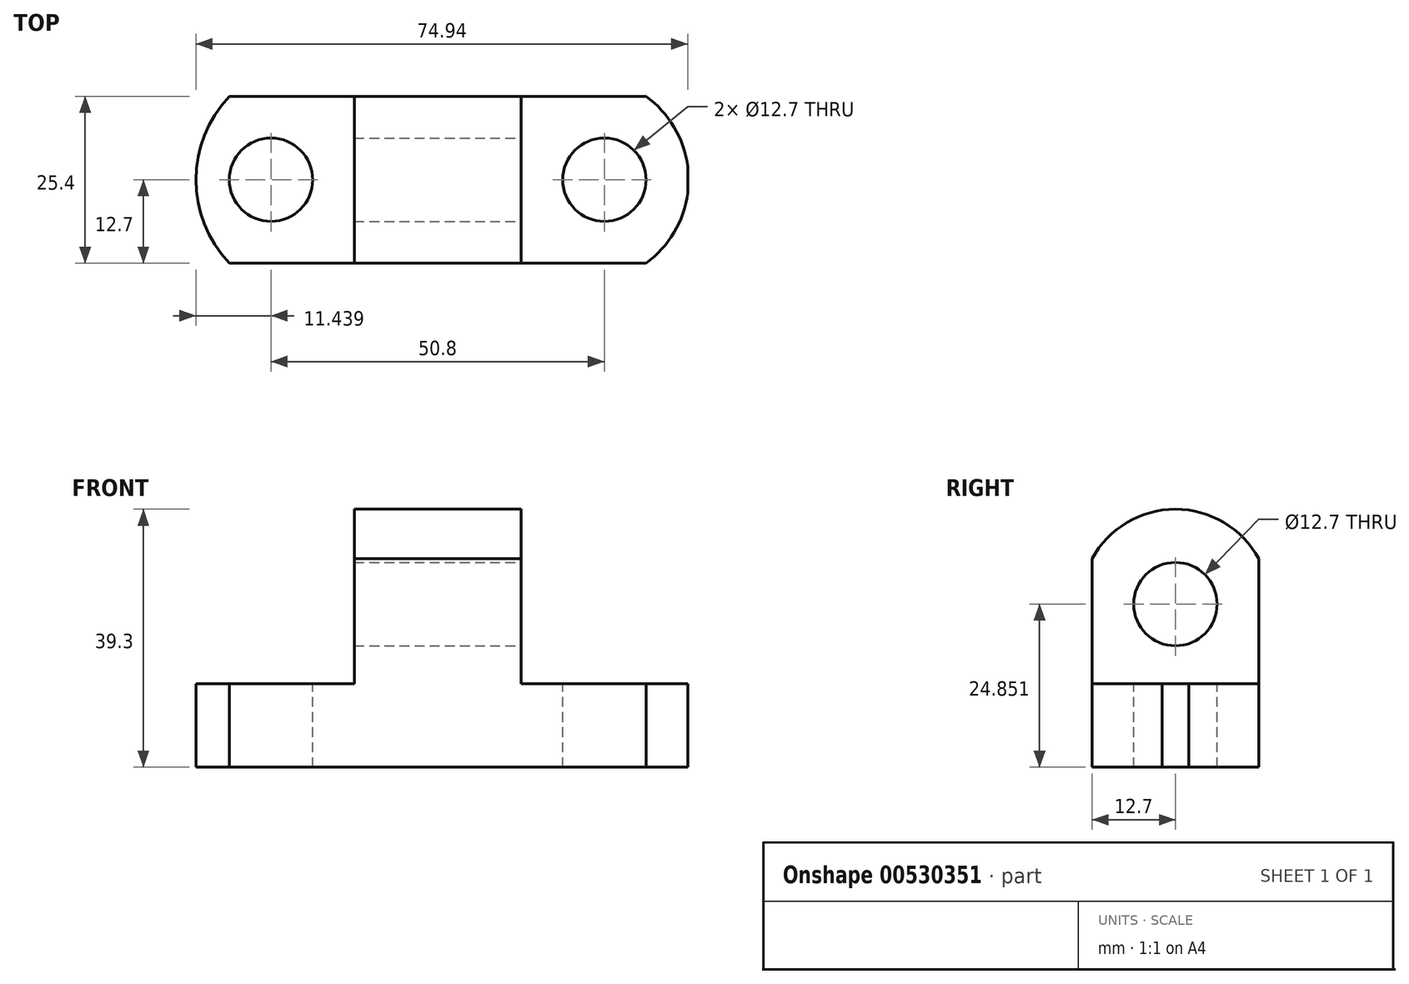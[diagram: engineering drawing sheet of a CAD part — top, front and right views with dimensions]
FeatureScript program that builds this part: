
annotation { "Feature Type Name" : "Feature", "Feature Type Description" : "" }
export const myFeature = defineFeature(function(context is Context, id is Id, definition is map)
    precondition{}
    {
        {
            var Q0;
            Q0=qCreatedBy(makeId("Front.planeOp"),FACE);
            var sketch = newSketch(context, id + "F0", { "sketchPlane" : qUnion([Q0])});
            skLineSegment(sketch, "E0", {"start": v(-46.07, 12.7) * mm, "end": v(-46.07, 0) * mm});
            skLineSegment(sketch, "E1", {"start": v(-46.07, 0) * mm, "end": v(30.13, 0) * mm});
            skLineSegment(sketch, "E2", {"start": v(30.13, 0) * mm, "end": v(30.13, 12.7) * mm});
            skLineSegment(sketch, "E3", {"start": v(30.13, 12.7) * mm, "end": v(4.73, 12.7) * mm});
            skLineSegment(sketch, "E4", {"start": v(4.73, 12.7) * mm, "end": v(4.73, 44.45) * mm});
            skLineSegment(sketch, "E5", {"start": v(4.73, 44.45) * mm, "end": v(-20.67, 44.45) * mm});
            skLineSegment(sketch, "E6", {"start": v(-20.67, 44.45) * mm, "end": v(-20.67, 12.7) * mm});
            skLineSegment(sketch, "E7", {"start": v(-20.67, 12.7) * mm, "end": v(-46.07, 12.7) * mm});
            skSolve(sketch);
        }
        {
            var Q0;
            Q0 = qSketchRegion(id + "F0", true);
            extrude(context, id + "F1", {"entities" : qUnion([Q0]), "depth" : 25.4 * mm, "offsetDistance" : 25.4 * mm});
        }
        {
            var Q0;
            Q0=makeQuery(id+"F1.opExtrude","SWEPT_FACE",FACE,{"disambiguationData":[OSD([sQuery(id+"F0.wireOp",EDGE,"E7")])]});
            var sketch = newSketch(context, id + "F2", { "sketchPlane" : qUnion([Q0])});
            skCircle(sketch, "E8", {"center": v(-33.37, -12.7) * mm, "radius": 6.35 * mm});
            skCircle(sketch, "E9", {"center": v(17.43, -12.7) * mm, "radius": 6.35 * mm});
            skSolve(sketch);
        }
        {
            var Q0;
            Q0=makeQuery(id+"F2.imprint","IMPRINT",FACE,{"disambiguationData":[TD([[makeQuery(id+"F2.imprint","IMPRINT",EDGE,{"derivedFrom":sQuery(id+"F2.wireOp",EDGE,"E9")}),1.0]])]});
            var Q1;
            Q1=makeQuery(id+"F2.imprint","IMPRINT",FACE,{"disambiguationData":[TD([[makeQuery(id+"F2.imprint","IMPRINT",EDGE,{"derivedFrom":sQuery(id+"F2.wireOp",EDGE,"E8")}),1.0]])]});
            extrude(context, id + "F3", {"entities" : qUnion([Q0, Q1]), "operationType" : NewBodyOperationType.REMOVE, "endBound" : BoundingType.THROUGH_ALL, "oppositeDirection" : true, "depth" : 25.4 * mm, "offsetDistance" : 25.4 * mm});
        }
        {
            var Q0;
            Q0=makeQuery(id+"F1.opExtrude","SWEPT_FACE",FACE,{"disambiguationData":[OSD([sQuery(id+"F0.wireOp",EDGE,"E4")])]});
            var sketch = newSketch(context, id + "F4", { "sketchPlane" : qUnion([Q0])});
            skArc(sketch, "E10", {"start": v(0, 31.75) * mm, "mid": v(-12.7, 39.3) * mm, "end": v(-25.4, 31.75) * mm});
            skCircle(sketch, "E11", {"center": v(-12.7, 24.85) * mm, "radius": 6.35 * mm});
            skSolve(sketch);
        }
        {
            var Q0;
            Q0 = qSketchRegion(id + "F4", true);
            var Q1;
            {var subQ0=sQuery(id+"F4.wireOp",EDGE,"E10");Q1=makeQuery(id+"F4.imprint","IMPRINT",FACE,{"disambiguationData":[TD([[makeQuery(id+"F4.imprint","IMPRINT",EDGE,{"derivedFrom":subQ0}),-1.0]])]});}
            extrude(context, id + "F5", {"entities" : qUnion([Q0, Q1]), "operationType" : NewBodyOperationType.REMOVE, "endBound" : BoundingType.THROUGH_ALL, "oppositeDirection" : true, "depth" : 25.4 * mm, "offsetDistance" : 25.4 * mm});
        }
        {
            var Q0;
            Q0=makeQuery(id+"F1.opExtrude","SWEPT_FACE",FACE,{"disambiguationData":[OSD([sQuery(id+"F0.wireOp",EDGE,"E7")])]});
            var sketch = newSketch(context, id + "F6", { "sketchPlane" : qUnion([Q0])});
            skArc(sketch, "E12", {"start": v(-39.72, 0) * mm, "mid": v(-44.8, -12.7) * mm, "end": v(-39.72, -25.4) * mm});
            skSolve(sketch);
        }
        {
            var Q0;
            Q0 = qSketchRegion(id + "F6", true);
            var Q1;
            {var subQ0=sQuery(id+"F6.wireOp",EDGE,"E12");Q1=makeQuery(id+"F6.imprint","IMPRINT",FACE,{"disambiguationData":[TD([[makeQuery(id+"F6.imprint","IMPRINT",EDGE,{"derivedFrom":subQ0}),-1.0]])]});}
            extrude(context, id + "F7", {"entities" : qUnion([Q0, Q1]), "operationType" : NewBodyOperationType.REMOVE, "endBound" : BoundingType.THROUGH_ALL, "oppositeDirection" : true, "depth" : 25.4 * mm, "offsetDistance" : 25.4 * mm});
        }
        {
            var Q0;
            Q0=makeQuery(id+"F1.opExtrude","SWEPT_FACE",FACE,{"disambiguationData":[OSD([sQuery(id+"F0.wireOp",EDGE,"E3")])]});
            var sketch = newSketch(context, id + "F8", { "sketchPlane" : qUnion([Q0])});
            skArc(sketch, "E13", {"start": v(23.78, -25.4) * mm, "mid": v(30.26, -12.7) * mm, "end": v(23.78, 0) * mm});
            skSolve(sketch);
        }
        {
            var Q0;
            Q0 = qSketchRegion(id + "F8", true);
            var Q1;
            {var subQ0=sQuery(id+"F8.wireOp",EDGE,"E13");var subQ1=sQuery(id+"F0.wireOp",EDGE,"E3");var subQ2=makeQuery(id+"F1.opExtrude","CAP_EDGE",EDGE,{"disambiguationData":[OSD([subQ1])],"isStart":true});var subQ3=makeQuery(id+"F8.imprint","INTERSECT",VERTEX,{"derivedFrom":[subQ2,subQ0]});Q1=makeQuery(id+"F8.imprint","IMPRINT",FACE,{"disambiguationData":[TD([[makeQuery(id+"F8.imprint","IMPRINT",EDGE,{"disambiguationData":[TD([[subQ3,1.0]])],"derivedFrom":subQ0}),-1.0]])]});}
            var Q2;
            {var subQ0=sQuery(id+"F8.wireOp",EDGE,"E13");var subQ1=sQuery(id+"F0.wireOp",EDGE,"E3");var subQ2=makeQuery(id+"F1.opExtrude","CAP_EDGE",EDGE,{"disambiguationData":[OSD([subQ1])],"isStart":false});var subQ3=makeQuery(id+"F8.imprint","INTERSECT",VERTEX,{"derivedFrom":[subQ2,subQ0]});Q2=makeQuery(id+"F8.imprint","IMPRINT",FACE,{"disambiguationData":[TD([[makeQuery(id+"F8.imprint","IMPRINT",EDGE,{"disambiguationData":[TD([[subQ3,-1.0]])],"derivedFrom":subQ0}),-1.0]])]});}
            extrude(context, id + "F9", {"entities" : qUnion([Q0, Q1, Q2]), "operationType" : NewBodyOperationType.REMOVE, "endBound" : BoundingType.THROUGH_ALL, "oppositeDirection" : true, "depth" : 25.4 * mm, "offsetDistance" : 25.4 * mm});
        }
    });
